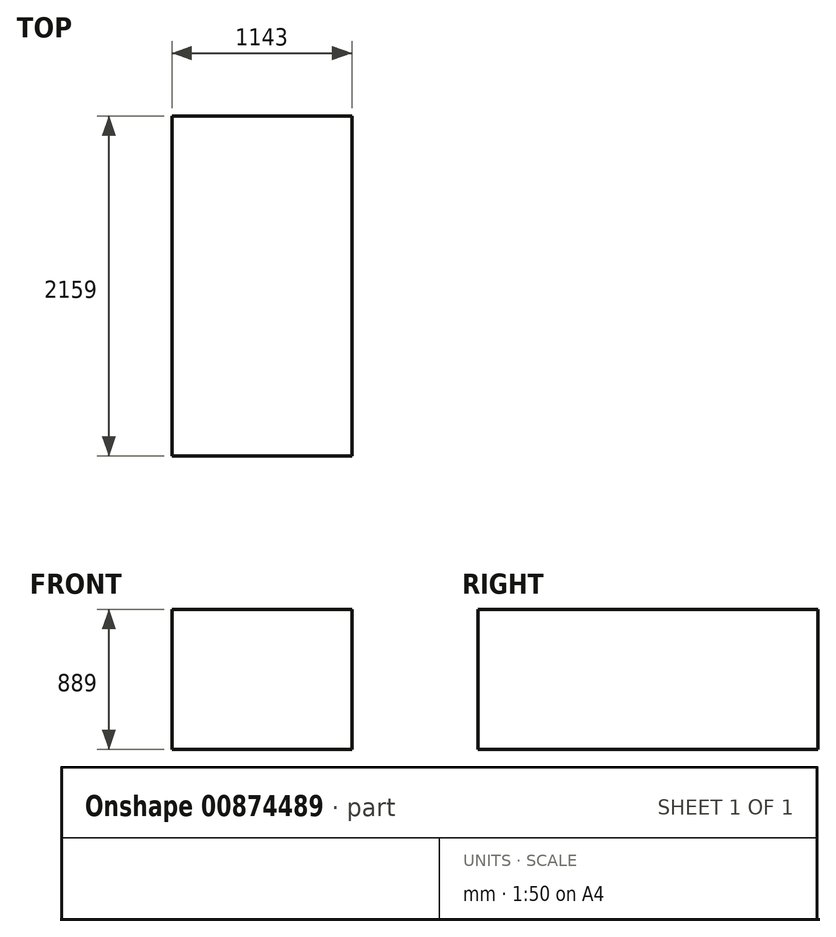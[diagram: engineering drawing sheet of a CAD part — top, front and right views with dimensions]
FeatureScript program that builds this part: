
annotation { "Feature Type Name" : "Feature", "Feature Type Description" : "" }
export const myFeature = defineFeature(function(context is Context, id is Id, definition is map)
    precondition{}
    {
        {
            var Q0;
            Q0=qCreatedBy(makeId("Front.planeOp"),FACE);
            var sketch = newSketch(context, id + "F0", { "sketchPlane" : qUnion([Q0])});
            skLineSegment(sketch, "E0.bottom", {"start": v(-571.5, 444.5) * mm, "end": v(571.5, 444.5) * mm});
            skLineSegment(sketch, "E0.top", {"start": v(-571.5, -444.5) * mm, "end": v(571.5, -444.5) * mm});
            skLineSegment(sketch, "E0.left", {"start": v(-571.5, 444.5) * mm, "end": v(-571.5, -444.5) * mm});
            skLineSegment(sketch, "E0.right", {"start": v(571.5, 444.5) * mm, "end": v(571.5, -444.5) * mm});
            skPoint(sketch, "E0.middle", {"position": v(0, 0) * mm});
            skSolve(sketch);
        }
        {
            var Q0;
            Q0=makeQuery(id+"F0.imprint","IMPRINT",FACE,{"disambiguationData":[TD([[makeQuery(id+"F0.imprint","IMPRINT",EDGE,{"derivedFrom":sQuery(id+"F0.wireOp",EDGE,"E0.bottom")}),-1.0]])]});
            extrude(context, id + "F1", {"entities" : qUnion([Q0]), "depth" : 2159 * mm, "offsetDistance" : 25.4 * mm});
        }
    });
